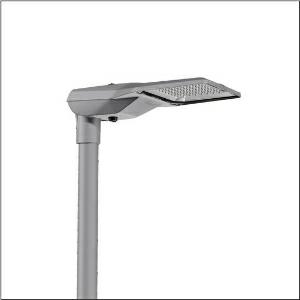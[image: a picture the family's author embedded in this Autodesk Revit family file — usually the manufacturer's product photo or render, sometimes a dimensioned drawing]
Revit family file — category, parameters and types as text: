
# Revit family: streetlight_sl_21_midi___st0_5a_5xe3b33t08mb_6d0d
name_source: partatom
category: Lighting Fixtures
units: mm (PartAtom-declared; Revit-internal decimal feet)

## family parameters
Cut with Voids When Loaded = No
Host = Face
Light Source = No
Part Type = Normal
Room Calculation Point = No
Round Connector Dimension = Use Diameter
Shared = No

## types (1)
- --- (1 x LED, 18270 lm, 136 W, 3000K)
    Apparent Load = 136 VA
    CIE Flux Codes = 41 75 97 100 100
    Color Rendering = 70
    Color Temperature = 3000K
    Default Elevation = 1800 mm
    Description = Streetlight SL 21 midi, mast luminaire, primary light control with lens, of PMMA, primary optical cover: cover, of toughened safety glass, transparent, light distribution: ST0.5a, light emission: direct distribution, primary light characteristic: asymmetric, installation type: side-entry, post-top, LED, High Power LED, rated luminous flux: 18.270lm, luminous efficacy: 134lm/W, light colour: 730, colour temperature: 3000K, control gear: D4i, control: overheat protection, constant luminous flux control, time-dependent luminous flux control, flexible luminous flux parameterisation, pre-setting: logarithmic dimming characteristic, mains connection: 230..240V, AC, 50/60Hz, start of lifetime: 136W, end of service life: 142W, reduction: 61W, luminaire housing, of diecast aluminium, powder-coated, Siteco® metallic grey (DB 702S), corrosivity category C5 mid according to DIN EN ISO 12944, please order mast flange separately, inclination adjustable: 0°, 5°, 10°, 15°, sealing non-destructively replaceable, multi-level sealing system, length: 644mm, width: 335mm, height: 110mm, mast flange for spigot size: 42mm (side-entry): 5XC10008XM4, 60/48mm (side-entry/post-top): 5XC10108XM2, 76/60mm (side-entry/post-top): 5XC10108XM1, mounting height: 4..8m, Smart Interface below and above, protection rating (complete): IP66, insulation class (complete): insulation class II (safety insulation), certification: CE, ENEC, ENEC+, VDE, impact resistance: IK10, permissible operating ambient temperature for outdoor applications: -40..+50°C, standard-compliant lighting for roads and squares, packaging unit: 1 piece

Light Distribution: ST0.5a
    Height = 111 mm
    Lamp = 1 x LED
    Lamp Light Flux = 18270 lm
    Lamp Power = 136 W
    Lamp count = 1
    Length = 644 mm
    Luminous efficacy = 134 lm/W
    Manufacturer = Siteco
    ModVariant = No
    Model = 5XE3B33T08MB
    Number of Poles = 1
    OnlyDefault = Yes
    Power Factor = 1
    Product Name = Streetlight SL 21 midi | ST0.5a
    Product group = mast luminaire | pylon top
    ProductGroupID = 6100
    Protection Class = Protection class II
    Protection Degree = IP 66
    RLX_Detail_Level = 1
    RLX_Emergency_Light_Flux = 0 lm
    RLX_Emergency_Type = 0
    RLX_Emergency_Type_DB = No
    RlxData = <blob elided: 37973 chars, md5=c14c22af>
    Socket = socket
    Standby Power = 0 W
    System Light Flux = 18270 lm
    System Power = 136 W
    Type Comments = factory setting: luminous flux: 100 % | dim-lin: 254 | 695 mA
    Type Image = l_1004304.jpg
    URL = http://relux.com
    VarID = @adj_191644
    Voltage = 0 V
    Weight = 0.00 kg
    Width = 336 mm

## geometry (parser evidence)
native form markers: Blend x4, Sweep x11
no freeform markers — native parametric forms only
